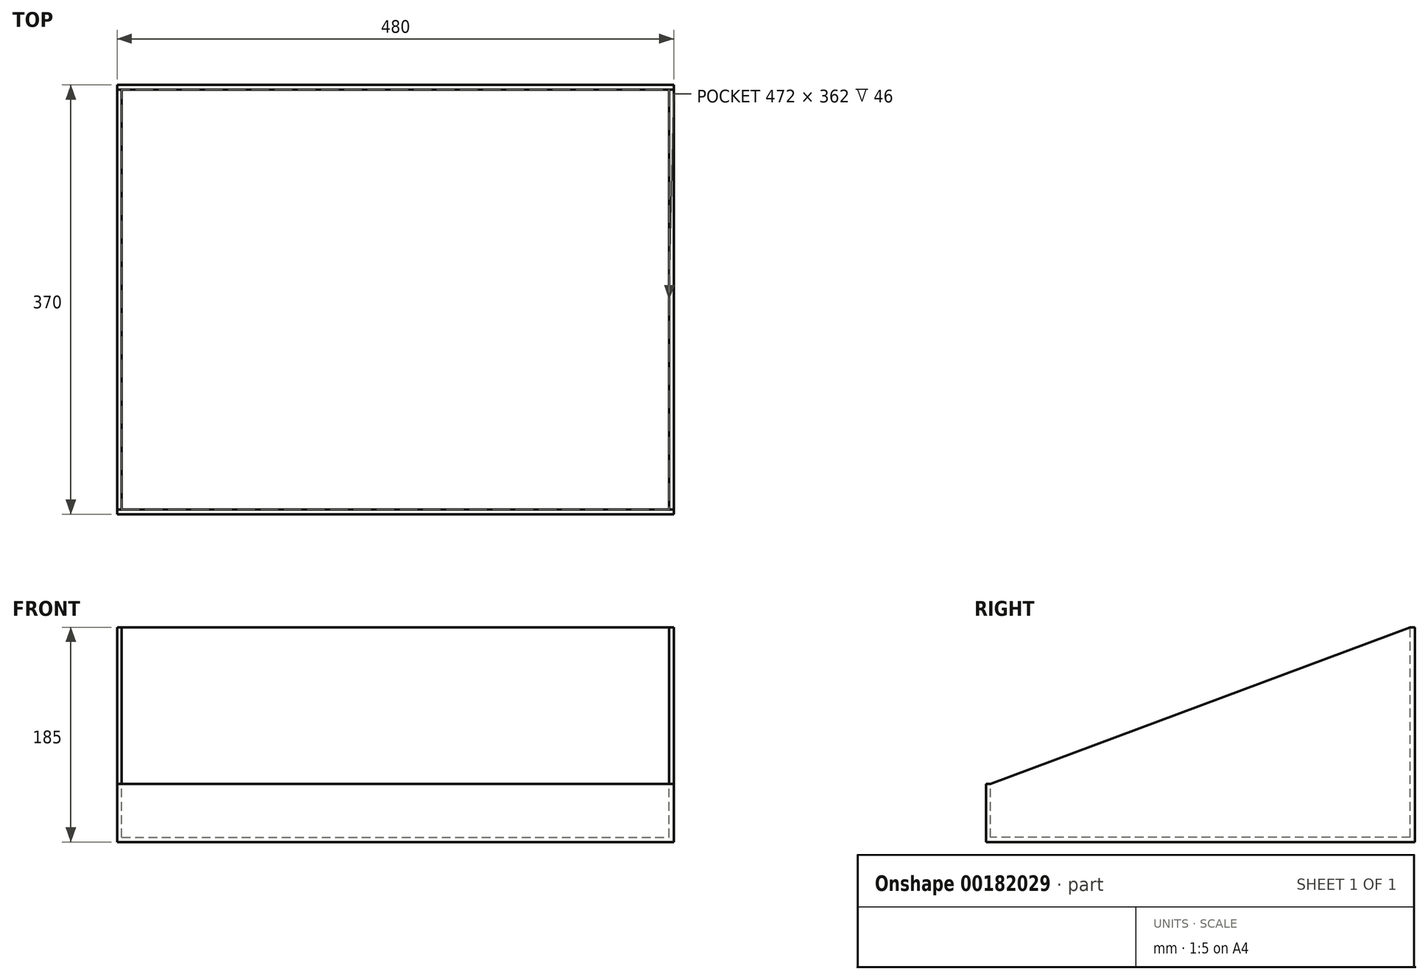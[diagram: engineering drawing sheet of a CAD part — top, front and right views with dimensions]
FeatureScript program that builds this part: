
annotation { "Feature Type Name" : "Feature", "Feature Type Description" : "" }
export const myFeature = defineFeature(function(context is Context, id is Id, definition is map)
    precondition{}
    {
        {
            var Q0;
            Q0=qCreatedBy(makeId("Front.planeOp"),FACE);
            var sketch = newSketch(context, id + "F0", { "sketchPlane" : qUnion([Q0])});
            skLineSegment(sketch, "E0.bottom", {"start": v(0, 0) * mm, "end": v(-480, 0) * mm});
            skLineSegment(sketch, "E0.top", {"start": v(0, 185) * mm, "end": v(-480, 185) * mm});
            skLineSegment(sketch, "E0.left", {"start": v(0, 0) * mm, "end": v(0, 185) * mm});
            skLineSegment(sketch, "E0.right", {"start": v(-480, 0) * mm, "end": v(-480, 185) * mm});
            skSolve(sketch);
        }
        {
            var Q0;
            Q0 = qSketchRegion(id + "F0", true);
            extrude(context, id + "F1", {"entities" : qUnion([Q0]), "oppositeDirection" : true, "depth" : 370 * mm});
        }
        {
            var Q0;
            Q0=qCreatedBy(makeId("Right.planeOp"),FACE);
            var sketch = newSketch(context, id + "F2", { "sketchPlane" : qUnion([Q0])});
            skLineSegment(sketch, "E1.0", {"start": v(370, 185) * mm, "end": v(0, 185) * mm, "construction": true});
            skLineSegment(sketch, "E2", {"start": v(4, 50) * mm, "end": v(366, 185) * mm});
            skLineSegment(sketch, "E3", {"start": v(366, 185) * mm, "end": v(0, 185) * mm});
            skLineSegment(sketch, "E4", {"start": v(0, 50) * mm, "end": v(4, 50) * mm});
            skLineSegment(sketch, "E5", {"start": v(0, 185) * mm, "end": v(0, 50) * mm});
            skSolve(sketch);
        }
        {
            var Q0;
            Q0 = qSketchRegion(id + "F2", true);
            extrude(context, id + "F3", {"entities" : qUnion([Q0]), "operationType" : NewBodyOperationType.REMOVE, "endBound" : BoundingType.UP_TO_NEXT, "oppositeDirection" : true, "depth" : 25 * mm});
        }
        {
            var Q0;
            Q0=qCreatedBy(makeId("Top.planeOp"),FACE);
            var Q1;
            Q1=makeQuery(id+"F3.boolean.opBoolean","COPY",VERTEX,{"derivedFrom":makeQuery(id+"F3.opExtrude","CAP_VERTEX",VERTEX,{"disambiguationData":[OSD([sQuery(id+"F2.wireOp",EDGE,"E2"),sQuery(id+"F2.wireOp",EDGE,"E3")])],"isStart":true})});
            cPlane(context, id + "F4", {"entities" : qUnion([Q0, Q1]), "cplaneType" : CPlaneType.PLANE_POINT, "offset" : 25 * mm, "width" : 150 * mm, "height" : 150 * mm});
        }
        {
            var Q0;
            Q0=qCreatedBy(id+"F4.planeOp",FACE);
            var sketch = newSketch(context, id + "F5", { "sketchPlane" : qUnion([Q0])});
            skLineSegment(sketch, "E6.0", {"start": v(0, 4) * mm, "end": v(0, 366) * mm, "construction": true});
            skLineSegment(sketch, "E6.1", {"start": v(-480, 366) * mm, "end": v(-480, 4) * mm, "construction": true});
            skLineSegment(sketch, "E7.0", {"start": v(-476, 366) * mm, "end": v(-476, 4) * mm, "construction": true});
            skLineSegment(sketch, "E8.0", {"start": v(-4, 4) * mm, "end": v(-4, 366) * mm, "construction": true});
            skLineSegment(sketch, "E9.bottom", {"start": v(-476, 366) * mm, "end": v(-4, 366) * mm});
            skLineSegment(sketch, "E9.top", {"start": v(-476, 4) * mm, "end": v(-4, 4) * mm});
            skLineSegment(sketch, "E9.left", {"start": v(-476, 366) * mm, "end": v(-476, 4) * mm});
            skLineSegment(sketch, "E9.right", {"start": v(-4, 366) * mm, "end": v(-4, 4) * mm});
            skSolve(sketch);
        }
        {
            var Q0;
            Q0 = qSketchRegion(id + "F5", true);
            extrude(context, id + "F6", {"entities" : qUnion([Q0]), "operationType" : NewBodyOperationType.REMOVE, "oppositeDirection" : true, "depth" : 181 * mm});
        }
    });
